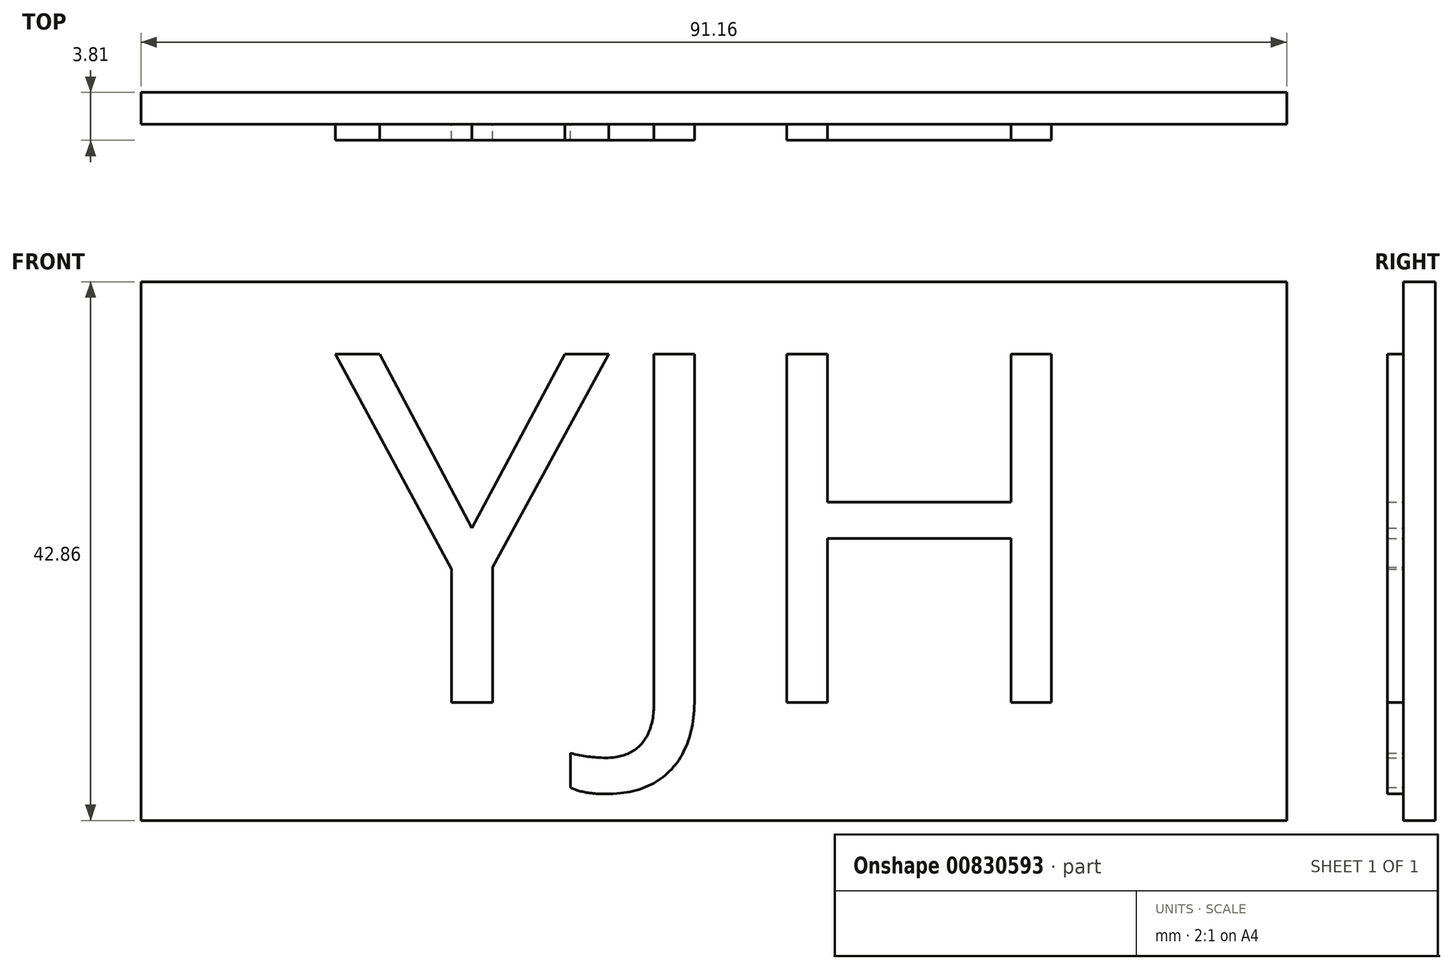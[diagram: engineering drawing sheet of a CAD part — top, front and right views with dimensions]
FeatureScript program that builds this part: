
annotation { "Feature Type Name" : "Feature", "Feature Type Description" : "" }
export const myFeature = defineFeature(function(context is Context, id is Id, definition is map)
    precondition{}
    {
        {
            var Q0;
            Q0=qCreatedBy(makeId("Front.planeOp"),FACE);
            var sketch = newSketch(context, id + "F0", { "sketchPlane" : qUnion([Q0])});
            skLineSegment(sketch, "E0.bottom", {"start": v(0, 0) * mm, "end": v(91.16, 0) * mm});
            skLineSegment(sketch, "E0.top", {"start": v(0, 42.86) * mm, "end": v(91.16, 42.86) * mm});
            skLineSegment(sketch, "E0.left", {"start": v(0, 0) * mm, "end": v(0, 42.86) * mm});
            skLineSegment(sketch, "E0.right", {"start": v(91.16, 0) * mm, "end": v(91.16, 42.86) * mm});
            skSolve(sketch);
        }
        {
            var Q0;
            Q0=makeQuery(id+"F0.imprint","IMPRINT",FACE,{"disambiguationData":[TD([[makeQuery(id+"F0.imprint","IMPRINT",EDGE,{"derivedFrom":sQuery(id+"F0.wireOp",EDGE,"E0.bottom")}),1.0]])]});
            extrude(context, id + "F1", {"entities" : qUnion([Q0]), "depth" : 2.54 * mm, "offsetDistance" : 25.4 * mm});
        }
        {
            var Q0;
            Q0=makeQuery(id+"F1.opExtrude","CAP_FACE",FACE,{"disambiguationData":[OSD([sQuery(id+"F0.wireOp",EDGE,"E0.bottom"),sQuery(id+"F0.wireOp",EDGE,"E0.top"),sQuery(id+"F0.wireOp",EDGE,"E0.left"),sQuery(id+"F0.wireOp",EDGE,"E0.right")])],"isStart":false});
            var sketch = newSketch(context, id + "F2", { "sketchPlane" : qUnion([Q0])});
            skText(sketch, "E1", { "text": "YJH", "fontName": "OpenSans-Regular.ttf"});
            const initialGuessF2  = {"E1": [0.01548, 0.0094, 1, 0, 0.02795]};
            skSetInitialGuess(sketch, initialGuessF2);
            skSolve(sketch);
        }
        {
            var Q0;
            Q0 = qSketchRegion(id + "F2", true);
            extrude(context, id + "F3", {"entities" : qUnion([Q0]), "operationType" : NewBodyOperationType.ADD, "depth" : 1.27 * mm, "offsetDistance" : 25.4 * mm});
        }
    });
